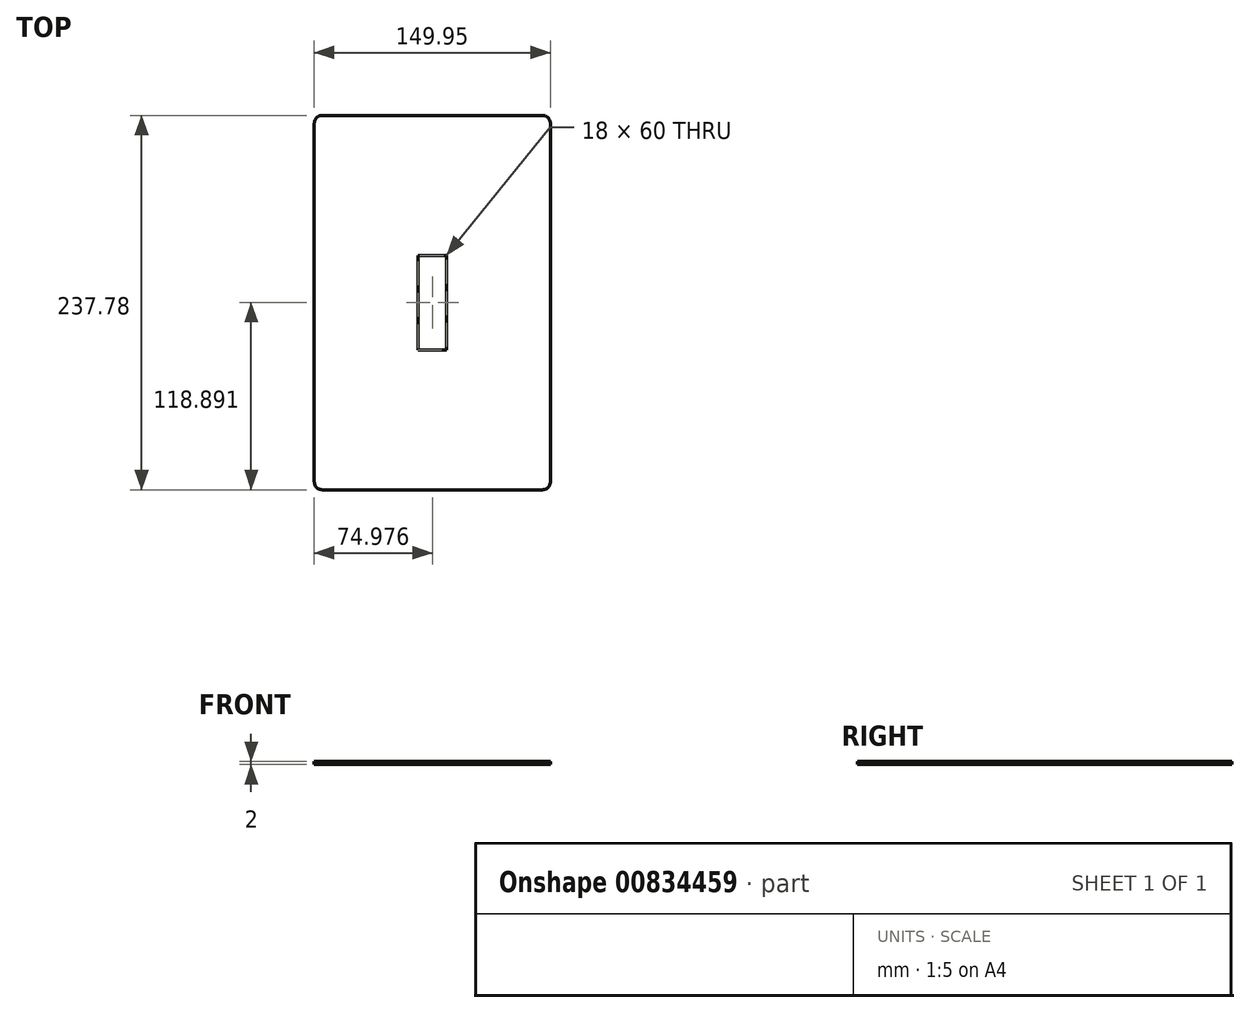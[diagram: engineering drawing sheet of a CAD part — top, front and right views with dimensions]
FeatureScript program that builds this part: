
annotation { "Feature Type Name" : "Feature", "Feature Type Description" : "" }
export const myFeature = defineFeature(function(context is Context, id is Id, definition is map)
    precondition{}
    {
        {
            var Q0;
            Q0=qCreatedBy(makeId("Top.planeOp"),FACE);
            var sketch = newSketch(context, id + "F0", { "sketchPlane" : qUnion([Q0])});
            skLineSegment(sketch, "E0.bottom", {"start": v(-75.68, 114.53) * mm, "end": v(-5.7, 114.53) * mm});
            skLineSegment(sketch, "E0.top", {"start": v(-75.68, -123.25) * mm, "end": v(-5.7, -123.25) * mm});
            skLineSegment(sketch, "E0.left", {"start": v(-80.68, 109.53) * mm, "end": v(-80.68, -4.36) * mm});
            skLineSegment(sketch, "E0.right", {"start": v(69.27, 109.53) * mm, "end": v(69.27, -4.36) * mm});
            skLineSegment(sketch, "E1", {"start": v(-5.7, 114.53) * mm, "end": v(64.27, 114.53) * mm});
            skLineSegment(sketch, "E2", {"start": v(-5.7, -123.25) * mm, "end": v(64.27, -123.25) * mm});
            skLineSegment(sketch, "E3", {"start": v(-80.68, -4.36) * mm, "end": v(-80.68, -118.25) * mm});
            skLineSegment(sketch, "E4", {"start": v(69.27, -4.36) * mm, "end": v(69.27, -118.25) * mm});
            skLineSegment(sketch, "E5", {"start": v(-5.7, 114.53) * mm, "end": v(-5.7, 25.64) * mm, "construction": true});
            skLineSegment(sketch, "E6", {"start": v(-5.7, -4.36) * mm, "end": v(-5.7, -34.36) * mm, "construction": true});
            skLineSegment(sketch, "E7", {"start": v(-5.7, 25.64) * mm, "end": v(-5.7, -4.36) * mm, "construction": true});
            skLineSegment(sketch, "E8", {"start": v(-5.7, -34.36) * mm, "end": v(-5.7, -123.25) * mm, "construction": true});
            skLineSegment(sketch, "E9", {"start": v(-5.7, 25.64) * mm, "end": v(3.3, 25.64) * mm});
            skLineSegment(sketch, "E10", {"start": v(-5.7, 25.64) * mm, "end": v(-14.7, 25.64) * mm});
            skLineSegment(sketch, "E11", {"start": v(-5.7, -34.36) * mm, "end": v(3.3, -34.36) * mm});
            skLineSegment(sketch, "E12", {"start": v(-5.7, -34.36) * mm, "end": v(-14.7, -34.36) * mm});
            skLineSegment(sketch, "E13", {"start": v(-14.7, 25.64) * mm, "end": v(-14.7, -34.36) * mm});
            skLineSegment(sketch, "E14", {"start": v(3.3, 25.64) * mm, "end": v(3.3, -34.36) * mm});
            skPoint(sketch, "E15.visualSharp", {"position": v(-80.68, 114.53) * mm});
            skArc(sketch, "E15.filletArc", {"start": v(-75.68, 114.53) * mm, "mid": v(-79.21, 113.06) * mm, "end": v(-80.68, 109.53) * mm});
            skPoint(sketch, "E16.visualSharp", {"position": v(69.27, 114.53) * mm});
            skArc(sketch, "E16.filletArc", {"start": v(69.27, 109.53) * mm, "mid": v(67.8, 113.06) * mm, "end": v(64.27, 114.53) * mm});
            skPoint(sketch, "E17.visualSharp", {"position": v(69.27, -123.25) * mm});
            skArc(sketch, "E17.filletArc", {"start": v(64.27, -123.25) * mm, "mid": v(67.8, -121.78) * mm, "end": v(69.27, -118.25) * mm});
            skPoint(sketch, "E18.visualSharp", {"position": v(-80.68, -123.25) * mm});
            skArc(sketch, "E18.filletArc", {"start": v(-80.68, -118.25) * mm, "mid": v(-79.21, -121.78) * mm, "end": v(-75.68, -123.25) * mm});
            skSolve(sketch);
        }
        {
            var Q0;
            Q0 = qSketchRegion(id + "F0", true);
            extrude(context, id + "F1", {"entities" : qUnion([Q0]), "depth" : 2 * mm, "offsetDistance" : 25 * mm});
        }
    });
